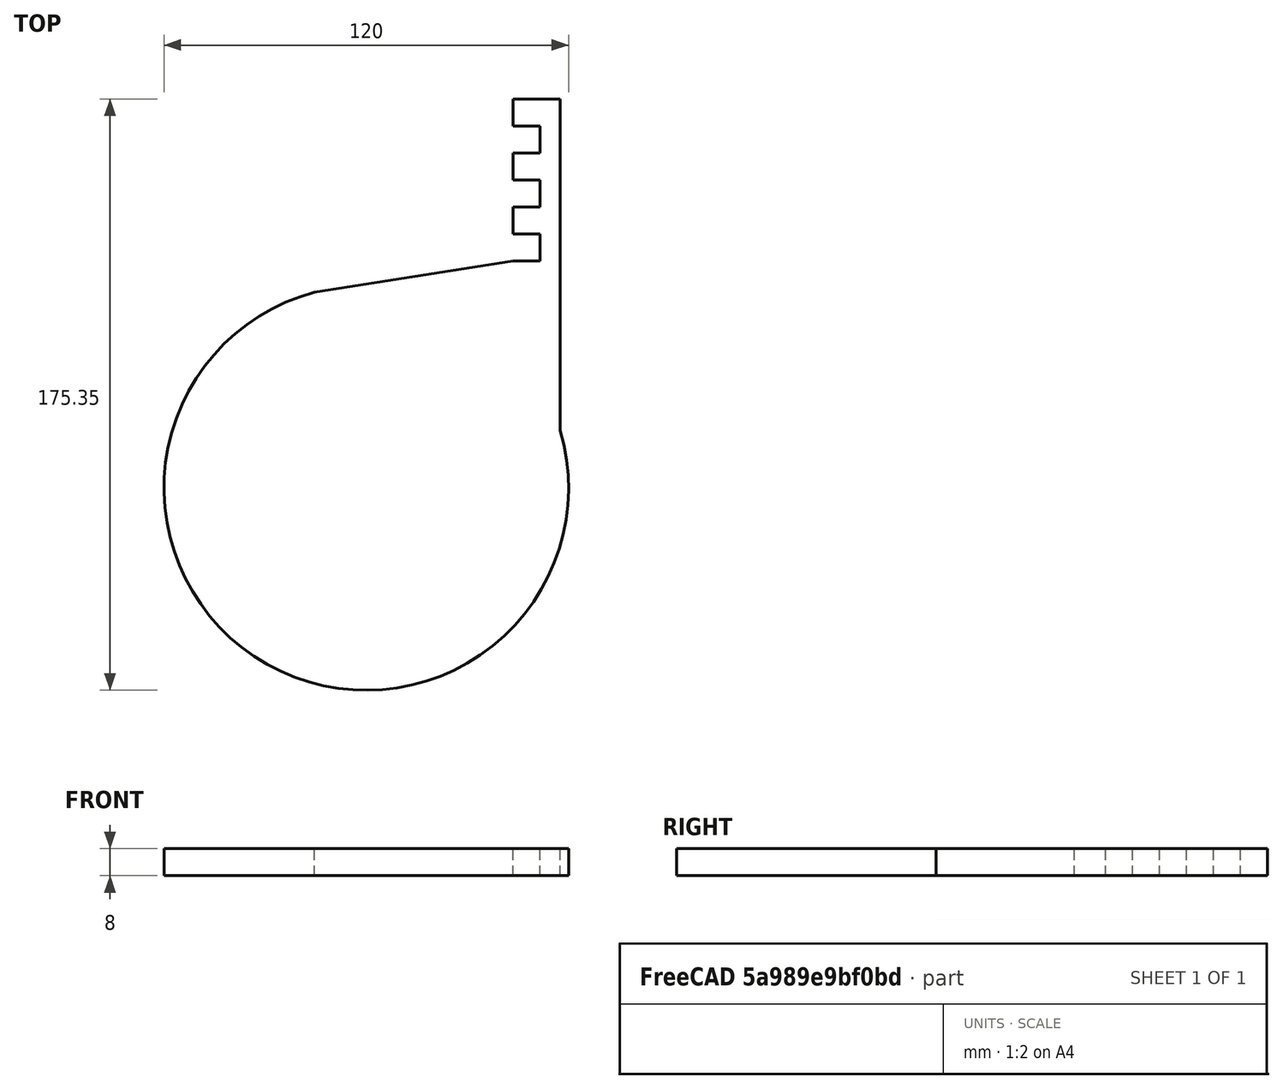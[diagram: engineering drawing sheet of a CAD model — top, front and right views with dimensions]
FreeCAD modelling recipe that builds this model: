
FCSTD DOCUMENT  (FreeCAD 0.14R3702 (Git))
Label: soporte_laser_tube
License: CC-BY 3.0
LicenseURL: http://creativecommons.org/licenses/by/3.0/
objects: Sketcher::SketchObject×1, PartDesign::Pad×1
note: 3 computed .brp shape members not serialized (recipe doc carries the construction recipe); baked Part::Feature solids carry a one-line shape summary decoded from their .brp

FEATURE [Sketcher::SketchObject] Sketch
  sketch-geometry (22):
    g0: LineSegment StartX=51.5303 StartY=115.351 StartZ=0 EndX=57.5303 EndY=115.351 EndZ=0
    g1: LineSegment StartX=57.5303 StartY=115.351 StartZ=0 EndX=57.5303 EndY=17.0372 EndZ=0
    g2: LineSegment [constr] StartX=-12 StartY=-30 StartZ=0 EndX=12 EndY=-30 EndZ=0
    g3: LineSegment [constr] StartX=12 StartY=-30 StartZ=0 EndX=12 EndY=-38 EndZ=0
    g4: LineSegment [constr] StartX=12 StartY=-38 StartZ=0 EndX=-12 EndY=-38 EndZ=0
    g5: LineSegment [constr] StartX=-12 StartY=-38 StartZ=0 EndX=-12 EndY=-30 EndZ=0
    g6: GeomPoint [constr] X=0 Y=0 Z=0
    g7: ArcOfCircle CenterX=0 CenterY=0 CenterZ=0 NormalX=0 NormalY=0 NormalZ=1 Radius=60 StartAngle=1.82972 EndAngle=6.5711
    g8: LineSegment StartX=51.5303 StartY=115.351 StartZ=0 EndX=43.5303 EndY=115.351 EndZ=0
    g9: LineSegment StartX=43.5303 StartY=115.351 StartZ=0 EndX=43.5303 EndY=107.351 EndZ=0
    g10: LineSegment StartX=43.5303 StartY=107.351 StartZ=0 EndX=51.5303 EndY=107.351 EndZ=0
    g11: LineSegment StartX=51.5303 StartY=107.351 StartZ=0 EndX=51.5303 EndY=99.3511 EndZ=0
    g12: LineSegment StartX=51.5303 StartY=99.3511 StartZ=0 EndX=43.5303 EndY=99.3511 EndZ=0
    g13: LineSegment StartX=43.5303 StartY=99.3511 StartZ=0 EndX=43.5303 EndY=91.3511 EndZ=0
    g14: LineSegment StartX=43.5303 StartY=91.3511 StartZ=0 EndX=51.5303 EndY=91.3511 EndZ=0
    g15: LineSegment StartX=51.5303 StartY=91.3511 StartZ=0 EndX=51.5303 EndY=83.3511 EndZ=0
    g16: LineSegment StartX=51.5303 StartY=83.3511 StartZ=0 EndX=43.5303 EndY=83.3511 EndZ=0
    g17: LineSegment StartX=43.5303 StartY=83.3511 StartZ=0 EndX=43.5303 EndY=75.3511 EndZ=0
    g18: LineSegment StartX=43.5303 StartY=75.3511 StartZ=0 EndX=51.5303 EndY=75.3511 EndZ=0
    g19: LineSegment StartX=51.5303 StartY=75.3511 StartZ=0 EndX=51.5303 EndY=67.3511 EndZ=0
    g20: LineSegment StartX=51.5303 StartY=67.3511 StartZ=0 EndX=43.5303 EndY=67.3511 EndZ=0
    g21: LineSegment StartX=43.5303 StartY=67.3511 StartZ=0 EndX=-15.3623 EndY=58 EndZ=0
  constraints (64):
    c: Horizontal(g0)
    c: Distance(g0) = 6
    c: Coincident(g1,g0)
    c: Vertical(g1)
    c: Coincident(g2,g3)
    c: Coincident(g3,g4)
    c: Coincident(g4,g5)
    c: Coincident(g5,g2)
    c: Horizontal(g2)
    c: Horizontal(g4)
    c: Vertical(g3)
    c: Vertical(g5)
    c: Distance(g5) = 8
    c: Distance(g2) = 24
    c: DistanceX(g-1,g4) = -12
    c: DistanceY(g-1,g2) = -30
    c: Coincident(g6,g-1)
    c: DistanceX(g-2,g0) = 57.5303
    c: Coincident(g7,g-1)
    c: Radius(g7) = 60
    c: Coincident(g0,g8)
    c: Horizontal(g8)
    c: Coincident(g8,g9)
    c: Vertical(g9)
    c: Coincident(g9,g10)
    c: Horizontal(g10)
    c: Coincident(g10,g11)
    c: Vertical(g11)
    c: Coincident(g11,g12)
    c: Horizontal(g12)
    c: Coincident(g12,g13)
    c: Vertical(g13)
    c: Coincident(g13,g14)
    c: Horizontal(g14)
    c: Coincident(g14,g15)
    c: Vertical(g15)
    c: Coincident(g15,g16)
    c: Horizontal(g16)
    c: Coincident(g16,g17)
    c: Vertical(g17)
    c: Coincident(g17,g18)
    c: Horizontal(g18)
    c: Coincident(g18,g19)
    c: Vertical(g19)
    c: Coincident(g19,g20)
    c: Horizontal(g20)
    c: Distance(g8) = 8
    c: Equal(g10,g9)
    c: Equal(g9,g8)
    c: Equal(g8,g11)
    c: Equal(g11,g12)
    c: Equal(g12,g13)
    c: Equal(g13,g14)
    c: Equal(g14,g16)
    c: Equal(g16,g15)
    c: Equal(g15,g17)
    c: Equal(g17,g18)
    c: Equal(g18,g19)
    c: Equal(g19,g20)
    c: Coincident(g21,g20)
    c: Coincident(g7,g21)
    c: Coincident(g7,g1)
    c: Coincident(g21,g7)
    c: DistanceY(g-1,g7) = 58
FEATURE [PartDesign::Pad] Pad
  Length = 8
  Length2 = 100
  Sketch = -> Sketch
  Type = 0
